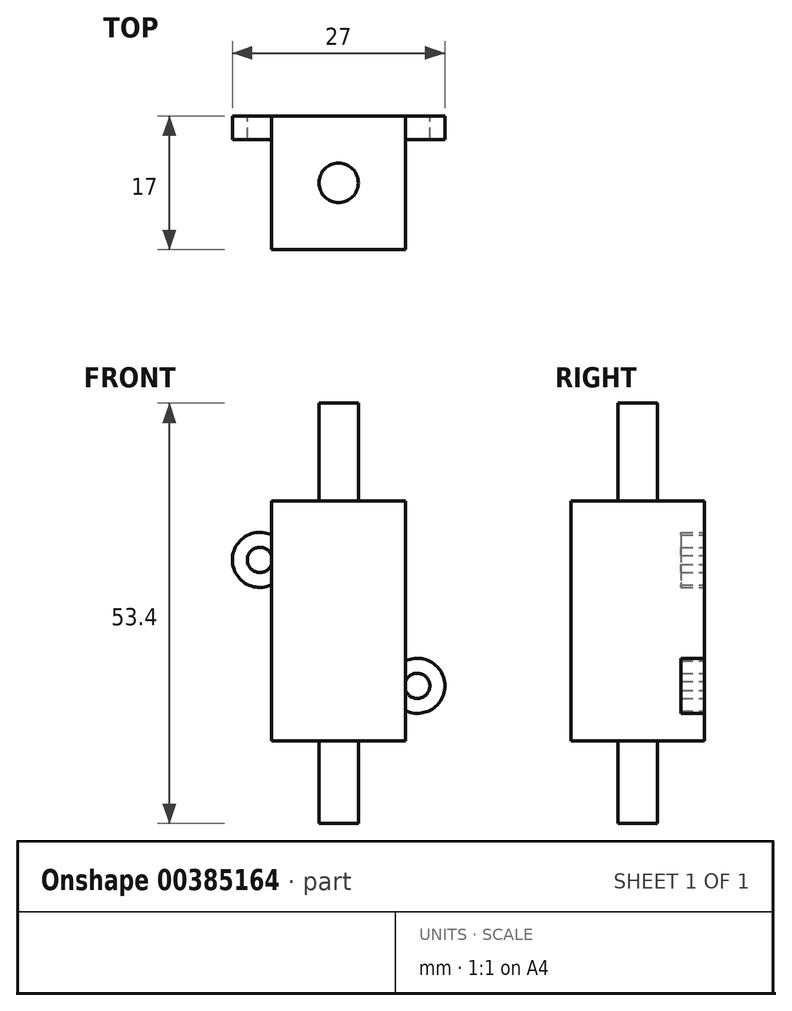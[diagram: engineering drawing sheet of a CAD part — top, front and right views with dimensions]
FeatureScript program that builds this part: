
annotation { "Feature Type Name" : "Feature", "Feature Type Description" : "" }
export const myFeature = defineFeature(function(context is Context, id is Id, definition is map)
    precondition{}
    {
        {
            var Q0;
            Q0=qCreatedBy(makeId("Front.planeOp"),FACE);
            var sketch = newSketch(context, id + "F0", { "sketchPlane" : qUnion([Q0])});
            skLineSegment(sketch, "E0.bottom", {"start": v(-8.5, 15.25) * mm, "end": v(8.5, 15.25) * mm});
            skLineSegment(sketch, "E0.top", {"start": v(-8.5, -15.25) * mm, "end": v(8.5, -15.25) * mm});
            skLineSegment(sketch, "E0.left", {"start": v(-8.5, 15.25) * mm, "end": v(-8.5, -15.25) * mm});
            skLineSegment(sketch, "E0.right", {"start": v(8.5, 15.25) * mm, "end": v(8.5, -15.25) * mm});
            skArc(sketch, "E1", {"start": v(-8.5, 8.3) * mm, "mid": v(-11.6, 7.75) * mm, "end": v(-8.5, 7.2) * mm});
            skArc(sketch, "E2.MirrorC", {"start": v(8.5, -8.8) * mm, "mid": v(11.6, -8.25) * mm, "end": v(8.5, -7.7) * mm});
            skArc(sketch, "E3", {"start": v(-8.5, 10.91) * mm, "mid": v(-13.5, 7.75) * mm, "end": v(-8.5, 4.59) * mm});
            skArc(sketch, "E4", {"start": v(8.5, -11.41) * mm, "mid": v(13.5, -8.25) * mm, "end": v(8.5, -5.09) * mm});
            skSolve(sketch);
        }
        {
            var Q0;
            {var subQ6=sQuery(id+"F0.wireOp",EDGE,"E0.bottom");Q0=makeQuery(id+"F0.imprint","IMPRINT",FACE,{"disambiguationData":[TD([[makeQuery(id+"F0.imprint","IMPRINT",EDGE,{"derivedFrom":subQ6}),-1.0]])]});}
            extrude(context, id + "F1", {"entities" : qUnion([Q0]), "depth" : 17 * mm, "offsetDistance" : 25 * mm});
        }
        {
            var Q0;
            {var subQ0=sQuery(id+"F0.wireOp",EDGE,"E1");Q0=makeQuery(id+"F0.imprint","IMPRINT",FACE,{"disambiguationData":[TD([[makeQuery(id+"F0.imprint","IMPRINT",EDGE,{"derivedFrom":subQ0}),-1.0]])]});}
            var Q1;
            {var subQ0=sQuery(id+"F0.wireOp",EDGE,"E2.MirrorC");Q1=makeQuery(id+"F0.imprint","IMPRINT",FACE,{"disambiguationData":[TD([[makeQuery(id+"F0.imprint","IMPRINT",EDGE,{"derivedFrom":subQ0}),-1.0]])]});}
            extrude(context, id + "F2", {"entities" : qUnion([Q0, Q1]), "operationType" : NewBodyOperationType.ADD, "depth" : 3 * mm, "offsetDistance" : 25 * mm});
        }
        {
            var Q0;
            Q0=makeQuery(id+"F1.opExtrude","SWEPT_FACE",FACE,{"disambiguationData":[OSD([sQuery(id+"F0.wireOp",EDGE,"E0.bottom")])]});
            var sketch = newSketch(context, id + "F3", { "sketchPlane" : qUnion([Q0])});
            skCircle(sketch, "E5", {"center": v(0, -8.5) * mm, "radius": 2.5 * mm});
            skPoint(sketch, "E5.centerSnap0", {"position": v(8.5, -8.5) * mm});
            skSolve(sketch);
        }
        {
            var Q0;
            Q0=makeQuery(id+"F3.imprint","IMPRINT",FACE,{"disambiguationData":[TD([[makeQuery(id+"F3.imprint","IMPRINT",EDGE,{"derivedFrom":sQuery(id+"F3.wireOp",EDGE,"E5")}),1.0]])]});
            extrude(context, id + "F4", {"entities" : qUnion([Q0]), "operationType" : NewBodyOperationType.ADD, "depth" : 12.4 * mm, "offsetDistance" : 25 * mm});
        }
        {
            var Q0;
            Q0=makeQuery(id+"F3.imprint","IMPRINT",FACE,{"disambiguationData":[TD([[makeQuery(id+"F3.imprint","IMPRINT",EDGE,{"derivedFrom":sQuery(id+"F3.wireOp",EDGE,"E5")}),1.0]])]});
            extrude(context, id + "F5", {"entities" : qUnion([Q0]), "operationType" : NewBodyOperationType.ADD, "oppositeDirection" : true, "depth" : 41 * mm, "offsetDistance" : 25 * mm});
        }
    });
